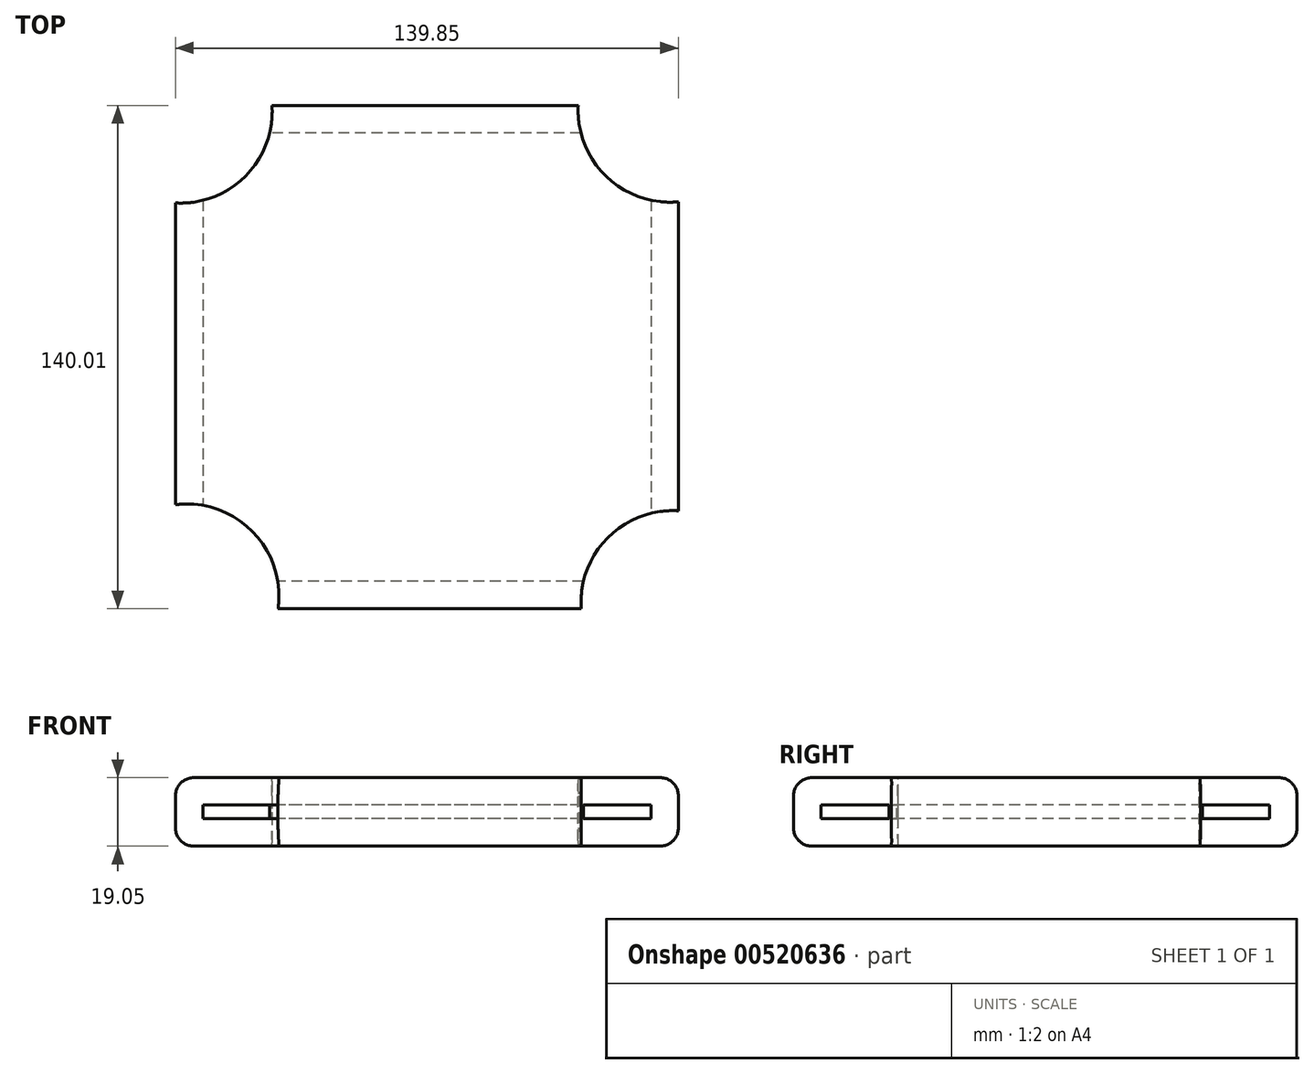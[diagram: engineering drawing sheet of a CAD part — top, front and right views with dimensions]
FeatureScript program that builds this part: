
annotation { "Feature Type Name" : "Feature", "Feature Type Description" : "" }
export const myFeature = defineFeature(function(context is Context, id is Id, definition is map)
    precondition{}
    {
        {
            var Q0;
            Q0=qCreatedBy(makeId("Top.planeOp"),FACE);
            var sketch = newSketch(context, id + "F0", { "sketchPlane" : qUnion([Q0])});
            skLineSegment(sketch, "E0.bottom", {"start": v(-62.2, -45.33) * mm, "end": v(77.64, -45.33) * mm});
            skLineSegment(sketch, "E0.top", {"start": v(-62.2, 94.68) * mm, "end": v(77.64, 94.68) * mm});
            skLineSegment(sketch, "E0.left", {"start": v(-62.2, -45.33) * mm, "end": v(-62.2, 94.68) * mm});
            skLineSegment(sketch, "E0.right", {"start": v(77.64, -45.33) * mm, "end": v(77.64, 94.68) * mm});
            skSolve(sketch);
        }
        {
            var Q0;
            Q0=makeQuery(id+"F0.imprint","IMPRINT",FACE,{"disambiguationData":[TD([[makeQuery(id+"F0.imprint","IMPRINT",EDGE,{"derivedFrom":sQuery(id+"F0.wireOp",EDGE,"E0.bottom")}),1.0]])]});
            extrude(context, id + "F1", {"entities" : qUnion([Q0]), "depth" : 19.05 * mm, "offsetDistance" : 25.4 * mm});
        }
        {
            var Q0;
            Q0=makeQuery(id+"F1.opExtrude","CAP_EDGE",EDGE,{"disambiguationData":[OSD([sQuery(id+"F0.wireOp",EDGE,"E0.bottom")])],"isStart":false});
            var Q1;
            Q1=makeQuery(id+"F1.opExtrude","CAP_EDGE",EDGE,{"disambiguationData":[OSD([sQuery(id+"F0.wireOp",EDGE,"E0.bottom")])],"isStart":true});
            var Q2;
            Q2=makeQuery(id+"F1.opExtrude","SWEPT_FACE",FACE,{"disambiguationData":[OSD([sQuery(id+"F0.wireOp",EDGE,"E0.left")])]});
            var Q3;
            Q3=makeQuery(id+"F1.opExtrude","CAP_EDGE",EDGE,{"disambiguationData":[OSD([sQuery(id+"F0.wireOp",EDGE,"E0.top")])],"isStart":false});
            var Q4;
            Q4=makeQuery(id+"F1.opExtrude","CAP_EDGE",EDGE,{"disambiguationData":[OSD([sQuery(id+"F0.wireOp",EDGE,"E0.top")])],"isStart":true});
            var Q5;
            Q5=makeQuery(id+"F1.opExtrude","CAP_EDGE",EDGE,{"disambiguationData":[OSD([sQuery(id+"F0.wireOp",EDGE,"E0.right")])],"isStart":false});
            var Q6;
            Q6=makeQuery(id+"F1.opExtrude","CAP_EDGE",EDGE,{"disambiguationData":[OSD([sQuery(id+"F0.wireOp",EDGE,"E0.right")])],"isStart":true});
            var Q7;
            Q7=makeQuery(id+"F1.opExtrude","SWEPT_EDGE",EDGE,{"disambiguationData":[OSD([sQuery(id+"F0.wireOp",EDGE,"E0.bottom"),sQuery(id+"F0.wireOp",EDGE,"E0.right")])]});
            var Q8;
            Q8=makeQuery(id+"F1.opExtrude","SWEPT_EDGE",EDGE,{"disambiguationData":[OSD([sQuery(id+"F0.wireOp",EDGE,"E0.top"),sQuery(id+"F0.wireOp",EDGE,"E0.right")])]});
            fillet(context, id + "F2", {"entities" : qUnion([Q0, Q1, Q2, Q3, Q4, Q5, Q6, Q7, Q8]), "radius" : 5.08 * mm, "tangentPropagation" : true, "allowEdgeOverflow" : false});
        }
        {
            var Q0;
            Q0=qCreatedBy(makeId("Top.planeOp"),FACE);
            var sketch = newSketch(context, id + "F3", { "sketchPlane" : qUnion([Q0])});
            skCircle(sketch, "E1", {"center": v(-58.98, -41.77) * mm, "radius": 25.57 * mm});
            skSolve(sketch);
        }
        {
            var Q0;
            Q0 = qSketchRegion(id + "F3", true);
            extrude(context, id + "F4", {"entities" : qUnion([Q0]), "operationType" : NewBodyOperationType.ADD, "depth" : 25.4 * mm, "offsetDistance" : 25.4 * mm});
        }
        {
            var Q0;
            Q0=makeQuery(id+"F4.opExtrude","CAP_FACE",FACE,{"disambiguationData":[OSD([sQuery(id+"F3.wireOp",EDGE,"E1")])],"isStart":false});
            extrude(context, id + "F5", {"entities" : qUnion([Q0]), "operationType" : NewBodyOperationType.REMOVE, "oppositeDirection" : true, "depth" : 25.4 * mm, "offsetDistance" : 25.4 * mm});
        }
        {
            var Q0;
            Q0=makeQuery(id+"F5.boolean.opBoolean","COPY",FACE,{"derivedFrom":makeQuery(id+"F5.opExtrude","SWEPT_FACE",FACE,{"disambiguationData":[OSD([sQuery(id+"F3.wireOp",EDGE,"E1")])]})});
            shell(context, id + "F6", {"entities" : qUnion([Q0]), "thickness" : 7.62 * mm});
        }
        {
            var Q0;
            Q0=qCreatedBy(makeId("Top.planeOp"),FACE);
            var sketch = newSketch(context, id + "F7", { "sketchPlane" : qUnion([Q0])});
            skCircle(sketch, "E2", {"center": v(-60.73, 92.94) * mm, "radius": 25.43 * mm});
            skSolve(sketch);
        }
        {
            var Q0;
            Q0 = qSketchRegion(id + "F7", true);
            extrude(context, id + "F8", {"entities" : qUnion([Q0]), "operationType" : NewBodyOperationType.ADD, "depth" : 25.4 * mm, "offsetDistance" : 25.4 * mm});
        }
        {
            var Q0;
            Q0=makeQuery(id+"F8.opExtrude","CAP_FACE",FACE,{"disambiguationData":[OSD([sQuery(id+"F7.wireOp",EDGE,"E2")])],"isStart":false});
            extrude(context, id + "F9", {"entities" : qUnion([Q0]), "operationType" : NewBodyOperationType.REMOVE, "oppositeDirection" : true, "depth" : 25.4 * mm, "offsetDistance" : 25.4 * mm});
        }
        {
            var Q0;
            Q0=qCreatedBy(makeId("Top.planeOp"),FACE);
            var sketch = newSketch(context, id + "F10", { "sketchPlane" : qUnion([Q0])});
            skCircle(sketch, "E3", {"center": v(76.06, -43.53) * mm, "radius": 25.48 * mm});
            skSolve(sketch);
        }
        {
            var Q0;
            Q0 = qSketchRegion(id + "F10", true);
            extrude(context, id + "F11", {"entities" : qUnion([Q0]), "operationType" : NewBodyOperationType.ADD, "depth" : 25.4 * mm, "offsetDistance" : 25.4 * mm});
        }
        {
            var Q0;
            Q0=makeQuery(id+"F11.opExtrude","CAP_FACE",FACE,{"disambiguationData":[OSD([sQuery(id+"F10.wireOp",EDGE,"E3")])],"isStart":false});
            extrude(context, id + "F12", {"entities" : qUnion([Q0]), "operationType" : NewBodyOperationType.REMOVE, "oppositeDirection" : true, "depth" : 25.4 * mm, "offsetDistance" : 25.4 * mm});
        }
        {
            var Q0;
            Q0=qCreatedBy(makeId("Top.planeOp"),FACE);
            var sketch = newSketch(context, id + "F13", { "sketchPlane" : qUnion([Q0])});
            skCircle(sketch, "E4", {"center": v(75.3, 93.3) * mm, "radius": 25.54 * mm});
            skSolve(sketch);
        }
        {
            var Q0;
            Q0 = qSketchRegion(id + "F13", true);
            extrude(context, id + "F14", {"entities" : qUnion([Q0]), "operationType" : NewBodyOperationType.ADD, "depth" : 25.4 * mm, "offsetDistance" : 25.4 * mm});
        }
        {
            var Q0;
            Q0=makeQuery(id+"F14.opExtrude","CAP_FACE",FACE,{"disambiguationData":[OSD([sQuery(id+"F13.wireOp",EDGE,"E4")])],"isStart":false});
            extrude(context, id + "F15", {"entities" : qUnion([Q0]), "operationType" : NewBodyOperationType.REMOVE, "oppositeDirection" : true, "depth" : 25.4 * mm, "offsetDistance" : 25.4 * mm});
        }
    });
